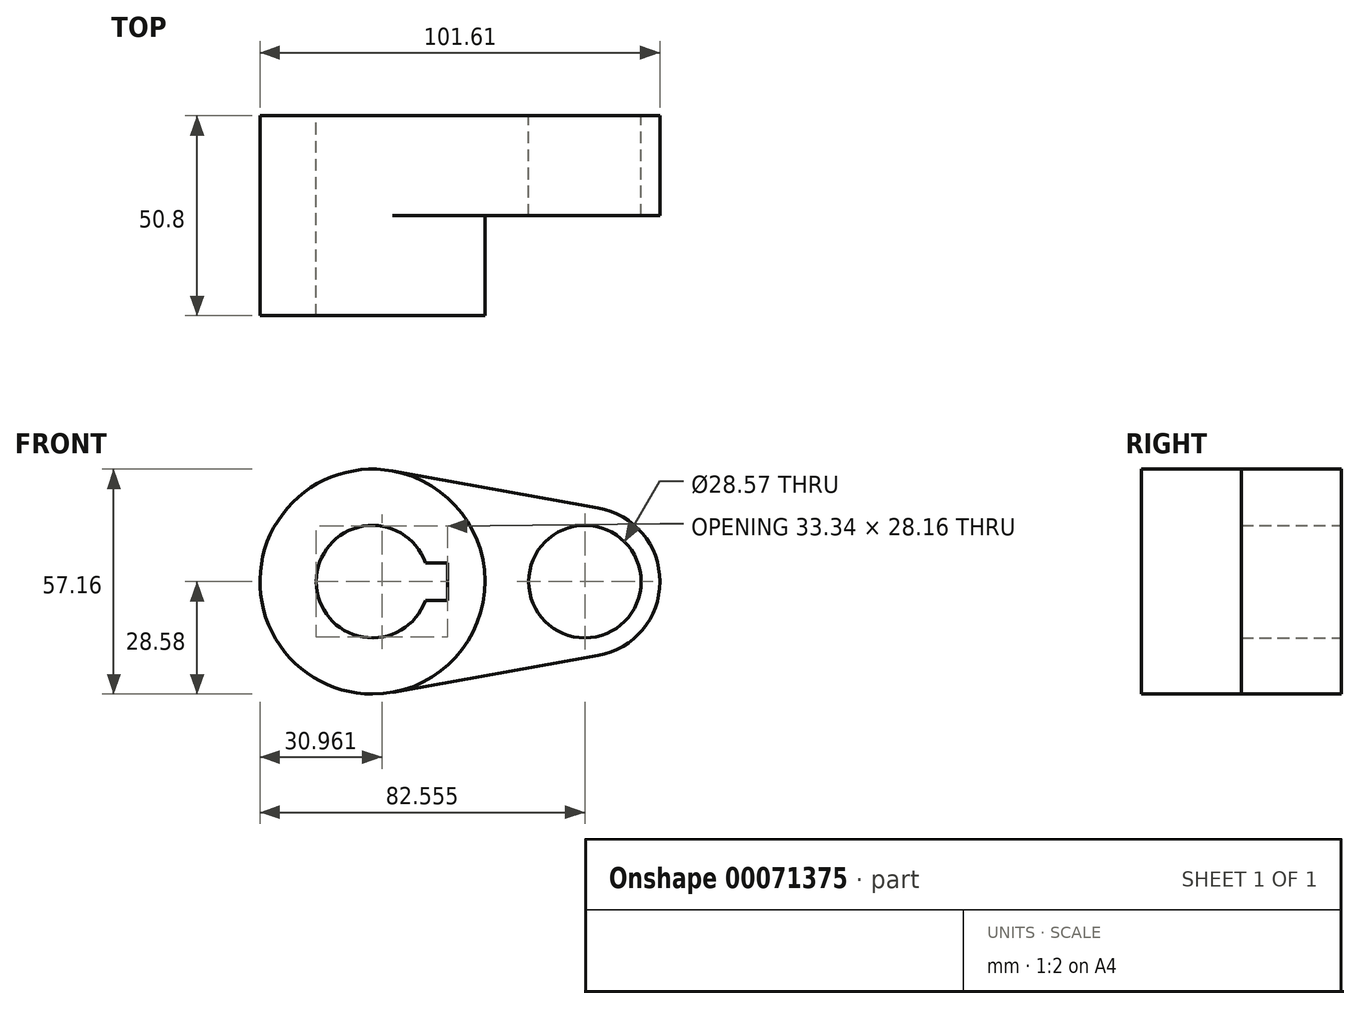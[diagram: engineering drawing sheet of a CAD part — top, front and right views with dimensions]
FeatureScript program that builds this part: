
annotation { "Feature Type Name" : "Feature", "Feature Type Description" : "" }
export const myFeature = defineFeature(function(context is Context, id is Id, definition is map)
    precondition{}
    {
        {
            var Q0;
            Q0=qCreatedBy(makeId("Front.planeOp"),FACE);
            var sketch = newSketch(context, id + "F0", { "sketchPlane" : qUnion([Q0])});
            skCircle(sketch, "E0", {"center": v(0, 0) * mm, "radius": 28.58 * mm});
            skCircle(sketch, "E1", {"center": v(53.98, 0) * mm, "radius": 19.05 * mm});
            skLineSegment(sketch, "E2", {"start": v(5.04, 28.13) * mm, "end": v(57.34, 18.75) * mm});
            skLineSegment(sketch, "E3", {"start": v(5.04, -28.13) * mm, "end": v(57.34, -18.75) * mm});
            skCircle(sketch, "E4", {"center": v(0, 0) * mm, "radius": 14.29 * mm});
            skCircle(sketch, "E5", {"center": v(53.98, 0) * mm, "radius": 14.29 * mm});
            skLineSegment(sketch, "E6.rect.bottom", {"start": v(19.05, 4.76) * mm, "end": v(-19.05, 4.76) * mm});
            skLineSegment(sketch, "E6.rect.top", {"start": v(19.05, -4.76) * mm, "end": v(-19.05, -4.76) * mm});
            skLineSegment(sketch, "E6.rect.left", {"start": v(19.05, 4.76) * mm, "end": v(19.05, -4.76) * mm});
            skLineSegment(sketch, "E6.rect.right", {"start": v(-19.05, 4.76) * mm, "end": v(-19.05, -4.76) * mm});
            skSolve(sketch);
        }
        {
            var Q0;
            Q0 = qSketchRegion(id + "F0", true);
            var Q1;
            {var subQ5=sQuery(id+"F0.wireOp",EDGE,"E6.rect.right");Q1=makeQuery(id+"F0.imprint","IMPRINT",FACE,{"disambiguationData":[TD([[makeQuery(id+"F0.imprint","IMPRINT",EDGE,{"derivedFrom":subQ5}),1.0]])]});}
            extrude(context, id + "F1", {"entities" : qUnion([Q0, Q1]), "depth" : 25.4 * mm});
        }
        {
            var Q0;
            {var subQ11=sQuery(id+"F0.wireOp",EDGE,"E6.rect.left");Q0=makeQuery(id+"F0.imprint","IMPRINT",FACE,{"disambiguationData":[TD([[makeQuery(id+"F0.imprint","IMPRINT",EDGE,{"derivedFrom":subQ11}),1.0]])]});}
            var Q1;
            {var subQ5=sQuery(id+"F0.wireOp",EDGE,"E6.rect.right");Q1=makeQuery(id+"F0.imprint","IMPRINT",FACE,{"disambiguationData":[TD([[makeQuery(id+"F0.imprint","IMPRINT",EDGE,{"derivedFrom":subQ5}),1.0]])]});}
            extrude(context, id + "F2", {"entities" : qUnion([Q0, Q1]), "operationType" : NewBodyOperationType.ADD, "depth" : 50.8 * mm});
        }
    });
